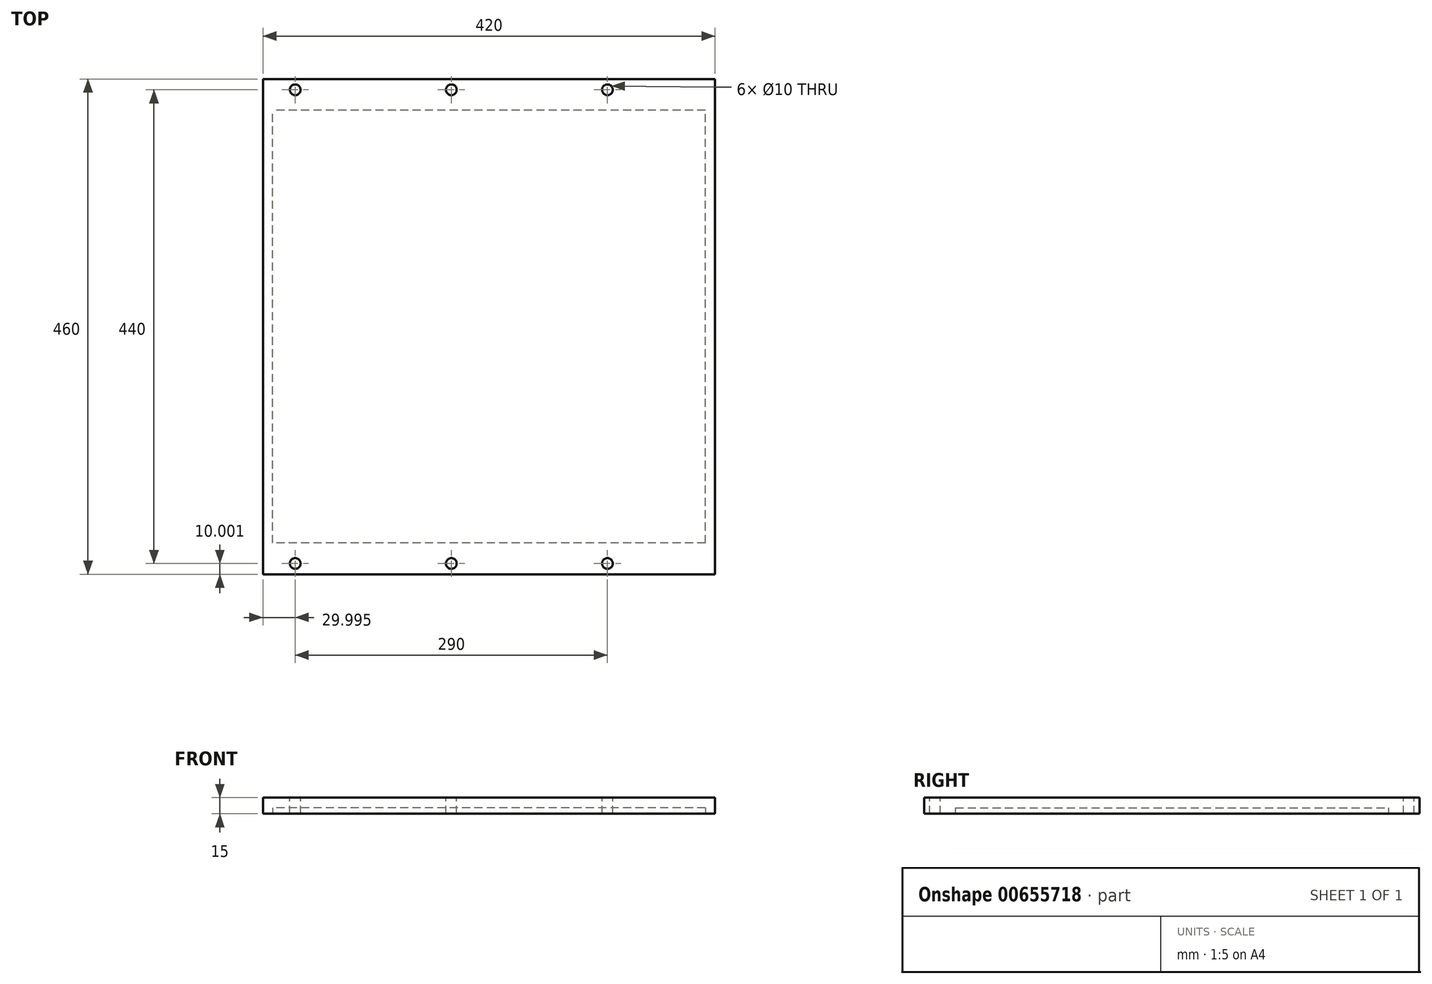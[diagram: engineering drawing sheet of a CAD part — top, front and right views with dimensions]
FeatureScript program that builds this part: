
annotation { "Feature Type Name" : "Feature", "Feature Type Description" : "" }
export const myFeature = defineFeature(function(context is Context, id is Id, definition is map)
    precondition{}
    {
        {
            var Q0;
            Q0=qCreatedBy(makeId("Top.planeOp"),FACE);
            var sketch = newSketch(context, id + "F0", { "sketchPlane" : qUnion([Q0])});
            skLineSegment(sketch, "E0.bottom", {"start": v(-74.43, -51.4) * mm, "end": v(345.57, -51.4) * mm});
            skLineSegment(sketch, "E0.top", {"start": v(-74.43, 408.6) * mm, "end": v(345.57, 408.6) * mm});
            skLineSegment(sketch, "E0.left", {"start": v(-74.43, -51.4) * mm, "end": v(-74.43, 408.6) * mm});
            skLineSegment(sketch, "E0.right", {"start": v(345.57, -51.4) * mm, "end": v(345.57, 408.6) * mm});
            skSolve(sketch);
        }
        {
            var Q0;
            Q0=makeQuery(id+"F0.imprint","IMPRINT",FACE,{"disambiguationData":[TD([[makeQuery(id+"F0.imprint","IMPRINT",EDGE,{"derivedFrom":sQuery(id+"F0.wireOp",EDGE,"E0.bottom")}),1.0]])]});
            extrude(context, id + "F1", {"entities" : qUnion([Q0]), "depth" : 15 * mm, "offsetDistance" : 25 * mm});
        }
        {
            var Q0;
            Q0=makeQuery(id+"F1.opExtrude","CAP_FACE",FACE,{"disambiguationData":[OSD([sQuery(id+"F0.wireOp",EDGE,"E0.bottom"),sQuery(id+"F0.wireOp",EDGE,"E0.top"),sQuery(id+"F0.wireOp",EDGE,"E0.left"),sQuery(id+"F0.wireOp",EDGE,"E0.right")])],"isStart":false});
            var sketch = newSketch(context, id + "F2", { "sketchPlane" : qUnion([Q0])});
            skCircle(sketch, "E1", {"center": v(245.57, -41.4) * mm, "radius": 5 * mm});
            skCircle(sketch, "E2", {"center": v(-44.43, -41.4) * mm, "radius": 5 * mm});
            skCircle(sketch, "E3", {"center": v(100.57, -41.4) * mm, "radius": 5 * mm});
            skLineSegment(sketch, "E4", {"start": v(-74.43, 178.6) * mm, "end": v(345.57, 178.6) * mm});
            skCircle(sketch, "E5.MirrorC", {"center": v(245.57, 398.6) * mm, "radius": 5 * mm});
            skCircle(sketch, "E6.MirrorC", {"center": v(100.57, 398.6) * mm, "radius": 5 * mm});
            skCircle(sketch, "E7.MirrorC", {"center": v(-44.43, 398.6) * mm, "radius": 5 * mm});
            skSolve(sketch);
        }
        {
            var Q0;
            Q0 = qSketchRegion(id + "F2", true);
            extrude(context, id + "F3", {"entities" : qUnion([Q0]), "operationType" : NewBodyOperationType.REMOVE, "oppositeDirection" : true, "depth" : 15 * mm, "offsetDistance" : 25 * mm});
        }
        {
            var Q0;
            Q0=makeQuery(id+"F1.opExtrude","CAP_FACE",FACE,{"disambiguationData":[OSD([sQuery(id+"F0.wireOp",EDGE,"E0.bottom"),sQuery(id+"F0.wireOp",EDGE,"E0.top"),sQuery(id+"F0.wireOp",EDGE,"E0.left"),sQuery(id+"F0.wireOp",EDGE,"E0.right")])],"isStart":true});
            var sketch = newSketch(context, id + "F4", { "sketchPlane" : qUnion([Q0])});
            skLineSegment(sketch, "E8.bottom", {"start": v(336.57, 22.4) * mm, "end": v(-65.43, 22.4) * mm});
            skLineSegment(sketch, "E8.top", {"start": v(336.57, -379.6) * mm, "end": v(-65.43, -379.6) * mm});
            skLineSegment(sketch, "E8.left", {"start": v(336.57, 22.4) * mm, "end": v(336.57, -379.6) * mm});
            skLineSegment(sketch, "E8.right", {"start": v(-65.43, 22.4) * mm, "end": v(-65.43, -379.6) * mm});
            skSolve(sketch);
        }
        {
            var Q0;
            Q0=makeQuery(id+"F4.imprint","IMPRINT",FACE,{"disambiguationData":[TD([[makeQuery(id+"F4.imprint","IMPRINT",EDGE,{"derivedFrom":sQuery(id+"F4.wireOp",EDGE,"E8.bottom")}),1.0]])]});
            extrude(context, id + "F5", {"entities" : qUnion([Q0]), "operationType" : NewBodyOperationType.REMOVE, "oppositeDirection" : true, "depth" : 5.5 * mm, "offsetDistance" : 25 * mm});
        }
    });
